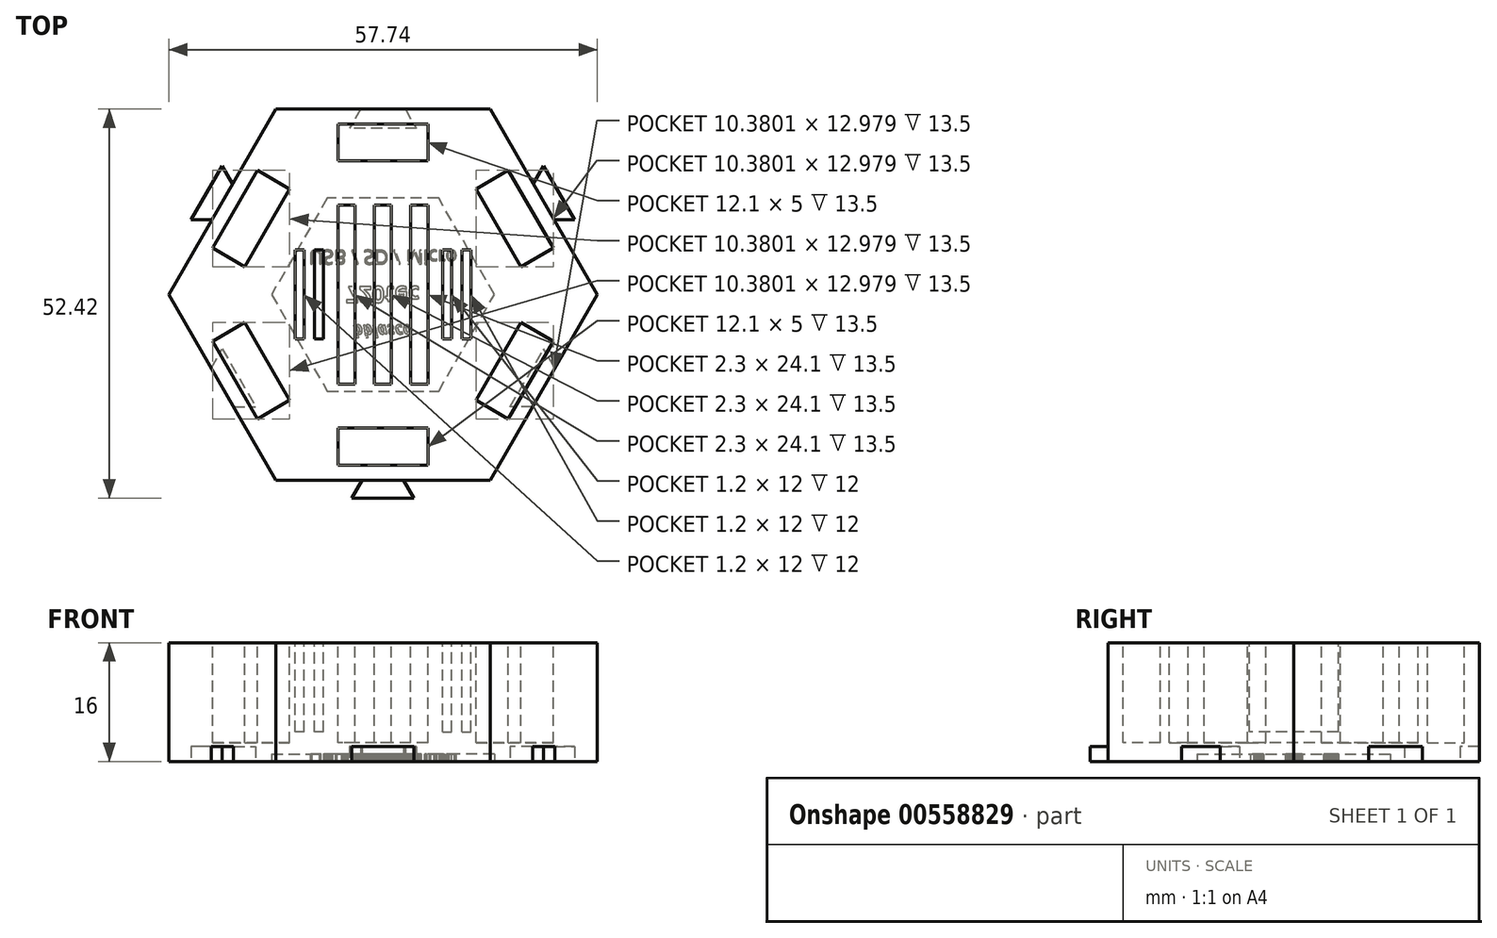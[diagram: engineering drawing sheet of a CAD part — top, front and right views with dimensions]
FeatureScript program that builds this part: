
annotation { "Feature Type Name" : "Feature", "Feature Type Description" : "" }
export const myFeature = defineFeature(function(context is Context, id is Id, definition is map)
    precondition{}
    {
        {
            var Q0;
            Q0=qCreatedBy(makeId("Top.planeOp"),FACE);
            var sketch = newSketch(context, id + "F0", { "sketchPlane" : qUnion([Q0])});
            skCircle(sketch, "E0.cCircle", {"center": v(0, 0) * mm, "radius": 25 * mm, "construction": true});
            skLineSegment(sketch, "E0.0", {"start": v(14.43, 25) * mm, "end": v(28.87, 0) * mm});
            skLineSegment(sketch, "E0.1", {"start": v(28.87, 0) * mm, "end": v(14.43, -25) * mm});
            skLineSegment(sketch, "E0.2", {"start": v(14.43, -25) * mm, "end": v(-14.43, -25) * mm});
            skLineSegment(sketch, "E0.3", {"start": v(-14.43, -25) * mm, "end": v(-28.87, 0) * mm});
            skLineSegment(sketch, "E0.4", {"start": v(-28.87, 0) * mm, "end": v(-16.25, 21.86) * mm});
            skLineSegment(sketch, "E0.5", {"start": v(-14.43, 25) * mm, "end": v(14.43, 25) * mm});
            skLineSegment(sketch, "E1", {"start": v(-21.65, -12.5) * mm, "end": v(21.65, 12.5) * mm, "construction": true});
            skLineSegment(sketch, "E2", {"start": v(21.65, -12.5) * mm, "end": v(-21.65, 12.5) * mm, "construction": true});
            skLineSegment(sketch, "E3", {"start": v(0, 25) * mm, "end": v(0, -25) * mm, "construction": true});
            skLineSegment(sketch, "E4", {"start": v(-23.15, -9.9) * mm, "end": v(-21.65, -7.3) * mm});
            skLineSegment(sketch, "E5", {"start": v(-21.65, -7.3) * mm, "end": v(-19.4, -11.2) * mm});
            skLineSegment(sketch, "E6.MirrorCS", {"start": v(-20.15, -15.1) * mm, "end": v(-17.15, -15.1) * mm});
            skLineSegment(sketch, "E7.MirrorCS", {"start": v(-17.15, -15.1) * mm, "end": v(-19.4, -11.2) * mm});
            skLineSegment(sketch, "E8", {"start": v(-2.8, -25) * mm, "end": v(-4.2, -27.42) * mm});
            skLineSegment(sketch, "E9", {"start": v(-4.2, -27.42) * mm, "end": v(0, -27.42) * mm});
            skLineSegment(sketch, "E10", {"start": v(0, -25) * mm, "end": v(2.8, -25) * mm});
            skLineSegment(sketch, "E11", {"start": v(2.8, -25) * mm, "end": v(4.2, -27.42) * mm});
            skLineSegment(sketch, "E12", {"start": v(4.2, -27.42) * mm, "end": v(0, -27.42) * mm});
            skLineSegment(sketch, "E13.trimOffspring", {"start": v(-16.25, 21.86) * mm, "end": v(-14.43, 25) * mm});
            skLineSegment(sketch, "E14.1.0", {"start": v(20.15, -15.1) * mm, "end": v(17.15, -15.1) * mm});
            skLineSegment(sketch, "E14.1.1", {"start": v(17.15, -15.1) * mm, "end": v(19.4, -11.2) * mm});
            skLineSegment(sketch, "E14.1.2", {"start": v(21.65, -7.3) * mm, "end": v(19.4, -11.2) * mm});
            skLineSegment(sketch, "E14.1.3", {"start": v(23.15, -9.9) * mm, "end": v(21.65, -7.3) * mm});
            skLineSegment(sketch, "E14.2.0", {"start": v(3, 25) * mm, "end": v(4.5, 22.4) * mm});
            skLineSegment(sketch, "E14.2.1", {"start": v(4.5, 22.4) * mm, "end": v(0, 22.4) * mm});
            skLineSegment(sketch, "E14.2.2", {"start": v(-4.5, 22.4) * mm, "end": v(0, 22.4) * mm});
            skLineSegment(sketch, "E14.2.3", {"start": v(-3, 25) * mm, "end": v(-4.5, 22.4) * mm});
            skLineSegment(sketch, "E15.1.0", {"start": v(25.85, 10.08) * mm, "end": v(23.75, 13.71) * mm});
            skLineSegment(sketch, "E15.1.1", {"start": v(23.05, 10.08) * mm, "end": v(25.85, 10.08) * mm});
            skLineSegment(sketch, "E15.1.2", {"start": v(20.25, 14.92) * mm, "end": v(21.65, 17.35) * mm});
            skLineSegment(sketch, "E15.1.3", {"start": v(21.65, 17.35) * mm, "end": v(23.75, 13.71) * mm});
            skLineSegment(sketch, "E15.2.0", {"start": v(-21.65, 17.35) * mm, "end": v(-23.75, 13.71) * mm});
            skLineSegment(sketch, "E15.2.1", {"start": v(-20.25, 14.92) * mm, "end": v(-21.65, 17.35) * mm});
            skLineSegment(sketch, "E15.2.2", {"start": v(-23.05, 10.08) * mm, "end": v(-25.85, 10.08) * mm});
            skLineSegment(sketch, "E15.2.3", {"start": v(-25.85, 10.08) * mm, "end": v(-23.75, 13.71) * mm});
            skSolve(sketch);
        }
        {
            var Q0;
            {var subQ0=sQuery(id+"F0.wireOp",EDGE,"9451e4d1-f90d-49d4-81d0-08b1ce128713");Q0=makeQuery(id+"F0.imprint","IMPRINT",FACE,{"disambiguationData":[TD([[makeQuery(id+"F0.imprint","IMPRINT",EDGE,{"derivedFrom":subQ0}),1.0]])]});}
            var Q1;
            {var subQ0=sQuery(id+"F0.wireOp",EDGE,"E8");Q1=makeQuery(id+"F0.imprint","IMPRINT",FACE,{"disambiguationData":[TD([[makeQuery(id+"F0.imprint","IMPRINT",EDGE,{"derivedFrom":subQ0}),1.0]])]});}
            var Q2;
            {var subQ11=sQuery(id+"F0.wireOp",EDGE,"E0.4");Q2=makeQuery(id+"F0.imprint","IMPRINT",FACE,{"disambiguationData":[TD([[makeQuery(id+"F0.imprint","IMPRINT",EDGE,{"derivedFrom":subQ11}),-1.0]])]});}
            var Q3;
            {var subQ1=sQuery(id+"F0.wireOp",EDGE,"9e98feac-76e8-4026-916c-793ea70c4b29");Q3=makeQuery(id+"F0.imprint","IMPRINT",FACE,{"disambiguationData":[TD([[makeQuery(id+"F0.imprint","IMPRINT",EDGE,{"derivedFrom":subQ1}),1.0]])]});}
            var Q4;
            Q4=makeQuery(id+"F0.imprint","IMPRINT",FACE,{"disambiguationData":[TD([[makeQuery(id+"F0.imprint","IMPRINT",EDGE,{"derivedFrom":sQuery(id+"F0.wireOp",EDGE,"d10c0532-f4be-419e-889c-b99b00964d50.2.0")}),-1.0]])]});
            var Q5;
            Q5=makeQuery(id+"F0.imprint","IMPRINT",FACE,{"disambiguationData":[TD([[makeQuery(id+"F0.imprint","IMPRINT",EDGE,{"derivedFrom":sQuery(id+"F0.wireOp",EDGE,"d10c0532-f4be-419e-889c-b99b00964d50.1.0")}),-1.0]])]});
            var Q6;
            Q6=makeQuery(id+"F0.imprint","IMPRINT",FACE,{"disambiguationData":[TD([[makeQuery(id+"F0.imprint","IMPRINT",EDGE,{"derivedFrom":sQuery(id+"F0.wireOp",EDGE,"E15.1.0")}),1.0]])]});
            var Q7;
            Q7=makeQuery(id+"F0.imprint","IMPRINT",FACE,{"disambiguationData":[TD([[makeQuery(id+"F0.imprint","IMPRINT",EDGE,{"derivedFrom":sQuery(id+"F0.wireOp",EDGE,"E15.2.0")}),1.0]])]});
            extrude(context, id + "F1", {"entities" : qUnion([Q0, Q1, Q2, Q3, Q4, Q5, Q6, Q7]), "depth" : 2 * mm, "offsetDistance" : 25 * mm});
        }
        {
            var Q0;
            Q0=makeQuery(id+"F1.opExtrude","CAP_FACE",FACE,{"disambiguationData":[OSD([sQuery(id+"F0.wireOp",EDGE,"E0.0"),sQuery(id+"F0.wireOp",EDGE,"E0.1"),sQuery(id+"F0.wireOp",EDGE,"E0.2"),sQuery(id+"F0.wireOp",EDGE,"E0.3"),sQuery(id+"F0.wireOp",EDGE,"E0.4"),sQuery(id+"F0.wireOp",EDGE,"E0.5"),sQuery(id+"F0.wireOp",EDGE,"E4"),sQuery(id+"F0.wireOp",EDGE,"E5"),sQuery(id+"F0.wireOp",EDGE,"E6.MirrorCS"),sQuery(id+"F0.wireOp",EDGE,"E7.MirrorCS"),sQuery(id+"F0.wireOp",EDGE,"E8"),sQuery(id+"F0.wireOp",EDGE,"E9"),sQuery(id+"F0.wireOp",EDGE,"E11"),sQuery(id+"F0.wireOp",EDGE,"E12"),sQuery(id+"F0.wireOp",EDGE,"50d66fe7-b7b8-4afa-a8e6-26ddb5301202"),sQuery(id+"F0.wireOp",EDGE,"f31b0c93-b72b-483d-9d13-11b0d4b3e3dc"),sQuery(id+"F0.wireOp",EDGE,"d1506e3d-a82a-4758-848e-6b189fab5584"),sQuery(id+"F0.wireOp",EDGE,"e0beb9cf-4cf0-4ad9-9de1-60ac7bd34435"),sQuery(id+"F0.wireOp",EDGE,"9451e4d1-f90d-49d4-81d0-08b1ce128713"),sQuery(id+"F0.wireOp",EDGE,"39f0793a-f1f0-4c94-b9c9-0f843c77a5cd"),sQuery(id+"F0.wireOp",EDGE,"4f74a49e-8b48-4a70-a3f3-9c3d992f8aed"),sQuery(id+"F0.wireOp",EDGE,"aaf5b410-3e02-488b-8bd8-8e2fa30f809d"),sQuery(id+"F0.wireOp",EDGE,"17fcc8c3-3659-474d-9c80-41cabe501613"),sQuery(id+"F0.wireOp",EDGE,"d6b08cdf-3ee8-41e2-9fd7-8cdca96f8f48"),sQuery(id+"F0.wireOp",EDGE,"adeda75a-8b2c-4688-a24d-cc9272189b78"),sQuery(id+"F0.wireOp",EDGE,"04944638-7935-4790-ad5a-2603b0dfc773"),sQuery(id+"F0.wireOp",EDGE,"9e98feac-76e8-4026-916c-793ea70c4b29"),sQuery(id+"F0.wireOp",EDGE,"37e32975-274e-4500-8d1c-8d1c18abe10c"),sQuery(id+"F0.wireOp",EDGE,"f71d59e6-90e3-4af3-bc8c-bc97efd2587d"),sQuery(id+"F0.wireOp",EDGE,"9624b2cd-eee6-426d-b3d3-c938f97f8664"),sQuery(id+"F0.wireOp",EDGE,"E13.trimOffspring")])],"isStart":false});
            var sketch = newSketch(context, id + "F2", { "sketchPlane" : qUnion([Q0])});
            skCircle(sketch, "E16.cCircle", {"center": v(0, 0) * mm, "radius": 25 * mm, "construction": true});
            skLineSegment(sketch, "E16.0", {"start": v(-14.43, -25) * mm, "end": v(-28.87, 0) * mm});
            skLineSegment(sketch, "E16.1", {"start": v(-28.87, 0) * mm, "end": v(-14.43, 25) * mm});
            skLineSegment(sketch, "E16.2", {"start": v(-14.43, 25) * mm, "end": v(14.43, 25) * mm});
            skLineSegment(sketch, "E16.3", {"start": v(14.43, 25) * mm, "end": v(28.87, 0) * mm});
            skLineSegment(sketch, "E16.4", {"start": v(28.87, 0) * mm, "end": v(14.43, -25) * mm});
            skLineSegment(sketch, "E16.5", {"start": v(14.43, -25) * mm, "end": v(-14.43, -25) * mm});
            skPoint(sketch, "E16.0.midPoint", {"position": v(-21.65, -12.5) * mm});
            skSolve(sketch);
        }
        {
            var Q0;
            Q0 = qSketchRegion(id + "F2", true);
            extrude(context, id + "F3", {"entities" : qUnion([Q0]), "operationType" : NewBodyOperationType.ADD, "depth" : 14 * mm, "offsetDistance" : 25 * mm});
        }
        {
            var Q0;
            Q0=makeQuery(id+"F3.opExtrude","CAP_FACE",FACE,{"disambiguationData":[OSD([sQuery(id+"F2.wireOp",EDGE,"E16.0"),sQuery(id+"F2.wireOp",EDGE,"E16.1"),sQuery(id+"F2.wireOp",EDGE,"E16.2"),sQuery(id+"F2.wireOp",EDGE,"E16.3"),sQuery(id+"F2.wireOp",EDGE,"E16.4"),sQuery(id+"F2.wireOp",EDGE,"E16.5")])],"isStart":false});
            var sketch = newSketch(context, id + "F4", { "sketchPlane" : qUnion([Q0])});
            skLineSegment(sketch, "E17", {"start": v(-6.05, -23) * mm, "end": v(6.05, -23) * mm});
            skLineSegment(sketch, "E18", {"start": v(6.05, -23) * mm, "end": v(6.05, -18) * mm});
            skLineSegment(sketch, "E19", {"start": v(6.05, -18) * mm, "end": v(-6.05, -18) * mm});
            skLineSegment(sketch, "E20", {"start": v(-6.05, -18) * mm, "end": v(-6.05, -23) * mm});
            skLineSegment(sketch, "E21", {"start": v(0, -25) * mm, "end": v(0, 2.92) * mm, "construction": true});
            skLineSegment(sketch, "E22", {"start": v(0, -18) * mm, "end": v(0, -23) * mm, "construction": true});
            skLineSegment(sketch, "E23.1.0", {"start": v(22.94, -6.26) * mm, "end": v(18.61, -3.76) * mm});
            skLineSegment(sketch, "E23.1.1", {"start": v(12.56, -14.24) * mm, "end": v(16.9, -16.74) * mm});
            skLineSegment(sketch, "E23.1.2", {"start": v(16.9, -16.74) * mm, "end": v(22.94, -6.26) * mm});
            skLineSegment(sketch, "E23.1.3", {"start": v(15.59, -9) * mm, "end": v(19.92, -11.5) * mm, "construction": true});
            skLineSegment(sketch, "E23.1.4", {"start": v(18.61, -3.76) * mm, "end": v(12.56, -14.24) * mm});
            skLineSegment(sketch, "E23.2.0", {"start": v(16.9, 16.74) * mm, "end": v(12.56, 14.24) * mm});
            skLineSegment(sketch, "E23.2.1", {"start": v(18.61, 3.76) * mm, "end": v(22.94, 6.26) * mm});
            skLineSegment(sketch, "E23.2.2", {"start": v(22.94, 6.26) * mm, "end": v(16.9, 16.74) * mm});
            skLineSegment(sketch, "E23.2.3", {"start": v(15.59, 9) * mm, "end": v(19.92, 11.5) * mm, "construction": true});
            skLineSegment(sketch, "E23.2.4", {"start": v(12.56, 14.24) * mm, "end": v(18.61, 3.76) * mm});
            skLineSegment(sketch, "E23.3.0", {"start": v(-6.05, 23) * mm, "end": v(-6.05, 18) * mm});
            skLineSegment(sketch, "E23.3.1", {"start": v(6.05, 18) * mm, "end": v(6.05, 23) * mm});
            skLineSegment(sketch, "E23.3.2", {"start": v(6.05, 23) * mm, "end": v(-6.05, 23) * mm});
            skLineSegment(sketch, "E23.3.3", {"start": v(0, 18) * mm, "end": v(0, 23) * mm, "construction": true});
            skLineSegment(sketch, "E23.3.4", {"start": v(-6.05, 18) * mm, "end": v(6.05, 18) * mm});
            skLineSegment(sketch, "E23.4.0", {"start": v(-22.94, 6.26) * mm, "end": v(-18.61, 3.76) * mm});
            skLineSegment(sketch, "E23.4.1", {"start": v(-12.56, 14.24) * mm, "end": v(-16.9, 16.74) * mm});
            skLineSegment(sketch, "E23.4.2", {"start": v(-16.9, 16.74) * mm, "end": v(-22.94, 6.26) * mm});
            skLineSegment(sketch, "E23.4.3", {"start": v(-15.59, 9) * mm, "end": v(-19.92, 11.5) * mm, "construction": true});
            skLineSegment(sketch, "E23.4.4", {"start": v(-18.61, 3.76) * mm, "end": v(-12.56, 14.24) * mm});
            skLineSegment(sketch, "E23.5.0", {"start": v(-16.9, -16.74) * mm, "end": v(-12.56, -14.24) * mm});
            skLineSegment(sketch, "E23.5.1", {"start": v(-18.61, -3.76) * mm, "end": v(-22.94, -6.26) * mm});
            skLineSegment(sketch, "E23.5.2", {"start": v(-22.94, -6.26) * mm, "end": v(-16.9, -16.74) * mm});
            skLineSegment(sketch, "E23.5.3", {"start": v(-15.59, -9) * mm, "end": v(-19.92, -11.5) * mm, "construction": true});
            skLineSegment(sketch, "E23.5.4", {"start": v(-12.56, -14.24) * mm, "end": v(-18.61, -3.76) * mm});
            skPoint(sketch, "E23.center", {"position": v(0, 0) * mm});
            skSolve(sketch);
        }
        {
            var Q0;
            Q0 = qSketchRegion(id + "F4", true);
            extrude(context, id + "F5", {"entities" : qUnion([Q0]), "operationType" : NewBodyOperationType.REMOVE, "oppositeDirection" : true, "depth" : 13.5 * mm, "offsetDistance" : 25 * mm});
        }
        {
            var Q0;
            Q0=makeQuery(id+"F3.opExtrude","CAP_FACE",FACE,{"disambiguationData":[OSD([sQuery(id+"F2.wireOp",EDGE,"E16.0"),sQuery(id+"F2.wireOp",EDGE,"E16.1"),sQuery(id+"F2.wireOp",EDGE,"E16.2"),sQuery(id+"F2.wireOp",EDGE,"E16.3"),sQuery(id+"F2.wireOp",EDGE,"E16.4"),sQuery(id+"F2.wireOp",EDGE,"E16.5")])],"isStart":false});
            var sketch = newSketch(context, id + "F6", { "sketchPlane" : qUnion([Q0])});
            skLineSegment(sketch, "E24", {"start": v(6.05, 18) * mm, "end": v(6.05, -18) * mm, "construction": true});
            skLineSegment(sketch, "E25", {"start": v(-6.05, 18) * mm, "end": v(-6.05, -18.03) * mm, "construction": true});
            skLineSegment(sketch, "E26.bottom", {"start": v(-3.75, 12.05) * mm, "end": v(-6.05, 12.05) * mm});
            skLineSegment(sketch, "E26.top", {"start": v(-3.75, -12.05) * mm, "end": v(-6.05, -12.05) * mm});
            skLineSegment(sketch, "E26.left", {"start": v(-3.75, 12.05) * mm, "end": v(-3.75, -12.05) * mm});
            skLineSegment(sketch, "E26.right", {"start": v(-6.05, 12.05) * mm, "end": v(-6.05, -12.05) * mm});
            skPoint(sketch, "E26.middle", {"position": v(-4.9, 0) * mm});
            skLineSegment(sketch, "E27.1.0.0", {"start": v(1.15, 12.05) * mm, "end": v(1.15, -12.05) * mm});
            skLineSegment(sketch, "E27.1.0.1", {"start": v(-1.15, 12.05) * mm, "end": v(-1.15, -12.05) * mm});
            skLineSegment(sketch, "E27.1.0.2", {"start": v(1.15, 12.05) * mm, "end": v(-1.15, 12.05) * mm});
            skPoint(sketch, "E27.1.0.3", {"position": v(0, 0) * mm});
            skLineSegment(sketch, "E27.1.0.4", {"start": v(1.15, -12.05) * mm, "end": v(-1.15, -12.05) * mm});
            skLineSegment(sketch, "E27.2.0.0", {"start": v(6.05, 12.05) * mm, "end": v(6.05, -12.05) * mm});
            skLineSegment(sketch, "E27.2.0.1", {"start": v(3.75, 12.05) * mm, "end": v(3.75, -12.05) * mm});
            skLineSegment(sketch, "E27.2.0.2", {"start": v(6.05, 12.05) * mm, "end": v(3.75, 12.05) * mm});
            skPoint(sketch, "E27.2.0.3", {"position": v(4.9, 0) * mm});
            skLineSegment(sketch, "E27.2.0.4", {"start": v(6.05, -12.05) * mm, "end": v(3.75, -12.05) * mm});
            skLineSegment(sketch, "E27.direction1", {"start": v(-6.05, -12.05) * mm, "end": v(-1.15, -12.05) * mm, "construction": true});
            skSolve(sketch);
        }
        {
            var Q0;
            Q0 = qSketchRegion(id + "F6", true);
            extrude(context, id + "F7", {"entities" : qUnion([Q0]), "operationType" : NewBodyOperationType.REMOVE, "oppositeDirection" : true, "depth" : 13.5 * mm, "offsetDistance" : 25 * mm});
        }
        {
            var Q0;
            Q0=makeQuery(id+"F3.opExtrude","CAP_FACE",FACE,{"disambiguationData":[OSD([sQuery(id+"F2.wireOp",EDGE,"E16.0"),sQuery(id+"F2.wireOp",EDGE,"E16.1"),sQuery(id+"F2.wireOp",EDGE,"E16.2"),sQuery(id+"F2.wireOp",EDGE,"E16.3"),sQuery(id+"F2.wireOp",EDGE,"E16.4"),sQuery(id+"F2.wireOp",EDGE,"E16.5")])],"isStart":false});
            var sketch = newSketch(context, id + "F8", { "sketchPlane" : qUnion([Q0])});
            skLineSegment(sketch, "E28.bottom", {"start": v(-8.05, 6) * mm, "end": v(-9.25, 6) * mm});
            skLineSegment(sketch, "E28.top", {"start": v(-8.05, -6) * mm, "end": v(-9.25, -6) * mm});
            skLineSegment(sketch, "E28.left", {"start": v(-8.05, 6) * mm, "end": v(-8.05, -6) * mm});
            skLineSegment(sketch, "E28.right", {"start": v(-9.25, 6) * mm, "end": v(-9.25, -6) * mm});
            skPoint(sketch, "E28.middle", {"position": v(-8.65, 0) * mm});
            skPoint(sketch, "E29.1.0.0", {"position": v(-11.25, 0) * mm});
            skLineSegment(sketch, "E29.1.0.1", {"start": v(-10.65, 6) * mm, "end": v(-10.65, -6) * mm});
            skLineSegment(sketch, "E29.1.0.2", {"start": v(-10.65, 6) * mm, "end": v(-11.85, 6) * mm});
            skLineSegment(sketch, "E29.1.0.3", {"start": v(-10.65, -6) * mm, "end": v(-11.85, -6) * mm});
            skLineSegment(sketch, "E29.1.0.4", {"start": v(-11.85, 6) * mm, "end": v(-11.85, -6) * mm});
            skLineSegment(sketch, "E29.direction1", {"start": v(-9.25, -6) * mm, "end": v(-11.85, -6) * mm, "construction": true});
            skLineSegment(sketch, "E30", {"start": v(0, 0) * mm, "end": v(0, 5.9) * mm, "construction": true});
            skLineSegment(sketch, "E31.MirrorCS", {"start": v(10.65, -6) * mm, "end": v(11.85, -6) * mm});
            skLineSegment(sketch, "E32.MirrorCS", {"start": v(10.65, 6) * mm, "end": v(10.65, -6) * mm});
            skPoint(sketch, "E33.MirrorP", {"position": v(11.25, 0) * mm});
            skLineSegment(sketch, "E34.MirrorCS", {"start": v(9.25, 6) * mm, "end": v(9.25, -6) * mm});
            skLineSegment(sketch, "E35.MirrorCS", {"start": v(11.85, 6) * mm, "end": v(11.85, -6) * mm});
            skLineSegment(sketch, "E36.MirrorCS", {"start": v(8.05, -6) * mm, "end": v(9.25, -6) * mm});
            skLineSegment(sketch, "E37.MirrorCS", {"start": v(8.05, 6) * mm, "end": v(9.25, 6) * mm});
            skPoint(sketch, "E38.MirrorP", {"position": v(8.65, 0) * mm});
            skLineSegment(sketch, "E39.MirrorCS", {"start": v(8.05, 6) * mm, "end": v(8.05, -6) * mm});
            skLineSegment(sketch, "E40.MirrorCS", {"start": v(10.65, 6) * mm, "end": v(11.85, 6) * mm});
            skSolve(sketch);
        }
        {
            var Q0;
            Q0 = qSketchRegion(id + "F8", true);
            extrude(context, id + "F9", {"entities" : qUnion([Q0]), "operationType" : NewBodyOperationType.REMOVE, "oppositeDirection" : true, "depth" : 12 * mm, "offsetDistance" : 25 * mm});
        }
        {
            var Q0;
            Q0=makeQuery(id+"F1.opExtrude","CAP_FACE",FACE,{"disambiguationData":[OSD([sQuery(id+"F0.wireOp",EDGE,"E0.0"),sQuery(id+"F0.wireOp",EDGE,"E0.1"),sQuery(id+"F0.wireOp",EDGE,"E0.2"),sQuery(id+"F0.wireOp",EDGE,"E0.3"),sQuery(id+"F0.wireOp",EDGE,"E0.4"),sQuery(id+"F0.wireOp",EDGE,"E0.5"),sQuery(id+"F0.wireOp",EDGE,"E4"),sQuery(id+"F0.wireOp",EDGE,"E5"),sQuery(id+"F0.wireOp",EDGE,"E6.MirrorCS"),sQuery(id+"F0.wireOp",EDGE,"E7.MirrorCS"),sQuery(id+"F0.wireOp",EDGE,"E8"),sQuery(id+"F0.wireOp",EDGE,"E9"),sQuery(id+"F0.wireOp",EDGE,"E11"),sQuery(id+"F0.wireOp",EDGE,"E12"),sQuery(id+"F0.wireOp",EDGE,"E13.trimOffspring"),sQuery(id+"F0.wireOp",EDGE,"763d033d-2536-437e-a8ba-70bd92ac569a.1.0"),sQuery(id+"F0.wireOp",EDGE,"763d033d-2536-437e-a8ba-70bd92ac569a.1.1"),sQuery(id+"F0.wireOp",EDGE,"763d033d-2536-437e-a8ba-70bd92ac569a.1.2"),sQuery(id+"F0.wireOp",EDGE,"763d033d-2536-437e-a8ba-70bd92ac569a.1.3"),sQuery(id+"F0.wireOp",EDGE,"763d033d-2536-437e-a8ba-70bd92ac569a.2.0"),sQuery(id+"F0.wireOp",EDGE,"763d033d-2536-437e-a8ba-70bd92ac569a.2.1"),sQuery(id+"F0.wireOp",EDGE,"763d033d-2536-437e-a8ba-70bd92ac569a.2.2"),sQuery(id+"F0.wireOp",EDGE,"763d033d-2536-437e-a8ba-70bd92ac569a.2.3"),sQuery(id+"F0.wireOp",EDGE,"d10c0532-f4be-419e-889c-b99b00964d50.1.0"),sQuery(id+"F0.wireOp",EDGE,"d10c0532-f4be-419e-889c-b99b00964d50.1.1"),sQuery(id+"F0.wireOp",EDGE,"d10c0532-f4be-419e-889c-b99b00964d50.1.2"),sQuery(id+"F0.wireOp",EDGE,"d10c0532-f4be-419e-889c-b99b00964d50.1.3"),sQuery(id+"F0.wireOp",EDGE,"d10c0532-f4be-419e-889c-b99b00964d50.2.0"),sQuery(id+"F0.wireOp",EDGE,"d10c0532-f4be-419e-889c-b99b00964d50.2.1"),sQuery(id+"F0.wireOp",EDGE,"d10c0532-f4be-419e-889c-b99b00964d50.2.2"),sQuery(id+"F0.wireOp",EDGE,"d10c0532-f4be-419e-889c-b99b00964d50.2.3")])],"isStart":true});
            var sketch = newSketch(context, id + "F10", { "sketchPlane" : qUnion([Q0])});
            skCircle(sketch, "E41.cCircle", {"center": v(0, 0) * mm, "radius": 13 * mm, "construction": true});
            skLineSegment(sketch, "E41.0", {"start": v(7.5, -13) * mm, "end": v(-7.5, -13) * mm});
            skLineSegment(sketch, "E41.1", {"start": v(-7.5, -13) * mm, "end": v(-15.01, 0) * mm});
            skLineSegment(sketch, "E41.2", {"start": v(-15.01, 0) * mm, "end": v(-7.5, 13) * mm});
            skLineSegment(sketch, "E41.3", {"start": v(-7.5, 13) * mm, "end": v(7.5, 13) * mm});
            skLineSegment(sketch, "E41.4", {"start": v(7.5, 13) * mm, "end": v(15.01, 0) * mm});
            skLineSegment(sketch, "E41.5", {"start": v(15.01, 0) * mm, "end": v(7.5, -13) * mm});
            skPoint(sketch, "E41.0.midPoint", {"position": v(0, -13) * mm});
            skSolve(sketch);
        }
        {
            var Q0;
            Q0 = qSketchRegion(id + "F10", true);
            extrude(context, id + "F11", {"entities" : qUnion([Q0]), "operationType" : NewBodyOperationType.REMOVE, "oppositeDirection" : true, "depth" : 1 * mm, "offsetDistance" : 25 * mm});
        }
        {
            var Q0;
            Q0=makeQuery(id+"F11.boolean.opBoolean","COPY",FACE,{"derivedFrom":makeQuery(id+"F11.opExtrude","CAP_FACE",FACE,{"disambiguationData":[OSD([sQuery(id+"F10.wireOp",EDGE,"E41.0"),sQuery(id+"F10.wireOp",EDGE,"E41.1"),sQuery(id+"F10.wireOp",EDGE,"E41.2"),sQuery(id+"F10.wireOp",EDGE,"E41.3"),sQuery(id+"F10.wireOp",EDGE,"E41.4"),sQuery(id+"F10.wireOp",EDGE,"E41.5")])],"isStart":false})});
            var sketch = newSketch(context, id + "F12", { "sketchPlane" : qUnion([Q0])});
            skText(sketch, "E42", { "text": "USB / SD / Micro", "fontName": "OpenSans-Regular.ttf"});
            skText(sketch, "E43", { "text": "720tec", "fontName": "OpenSans-Bold.ttf"});
            skText(sketch, "E44", { "text": "bblasco", "fontName": "OpenSans-BoldItalic.ttf"});
            const initialGuessF12  = {"E42": [-0.01, -0.00598, 1, 0, 0.00189], "E43": [-0.005, -0.0011, 1, 0, 0.0022], "E44": [-0.004, 0.0041, 1, 0, 0.00158]};
            skSetInitialGuess(sketch, initialGuessF12);
            skSolve(sketch);
        }
        {
            var Q0;
            Q0 = qSketchRegion(id + "F12", true);
            extrude(context, id + "F13", {"entities" : qUnion([Q0]), "operationType" : NewBodyOperationType.ADD, "depth" : 1 * mm, "offsetDistance" : 25 * mm});
        }
    });
